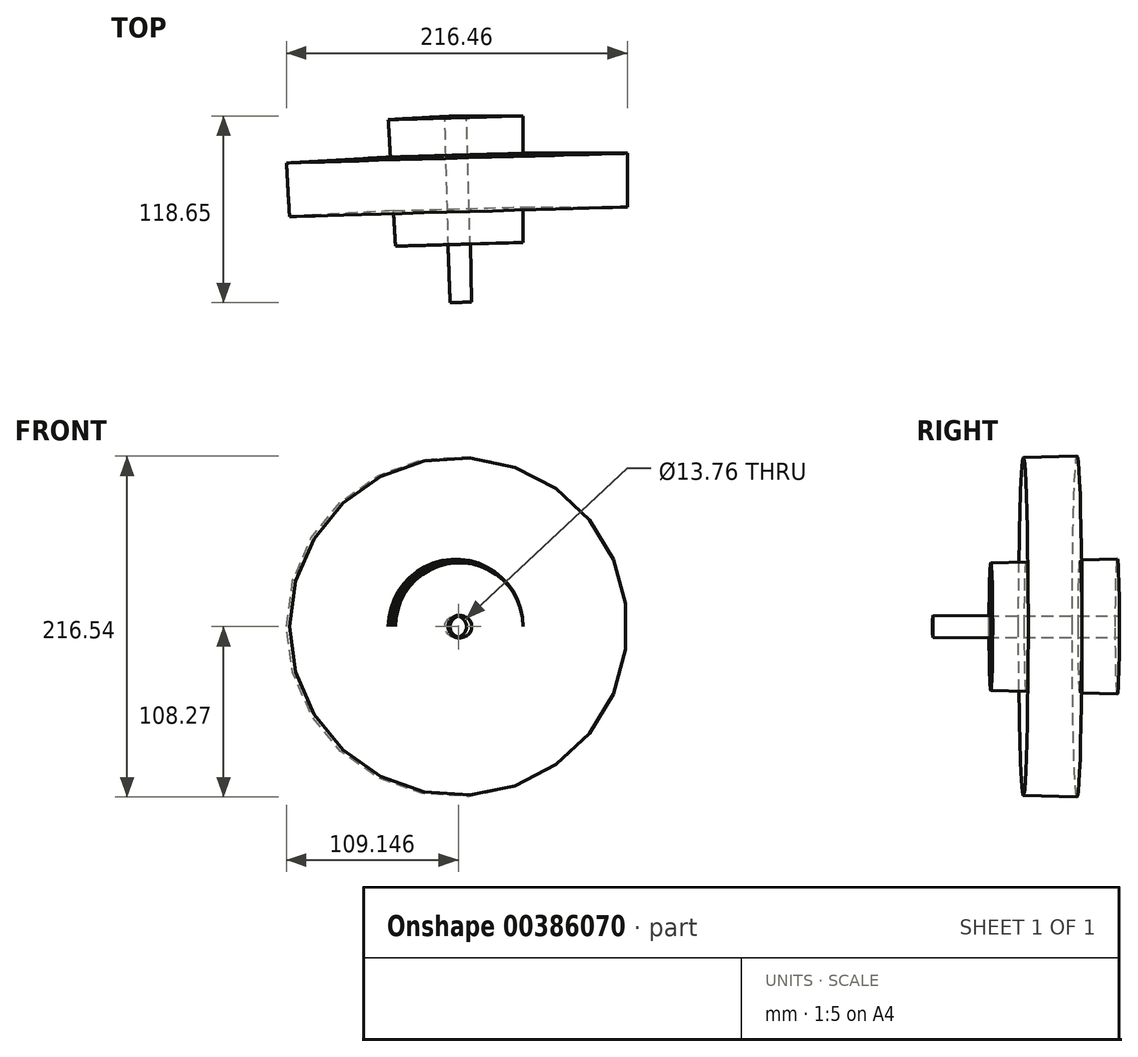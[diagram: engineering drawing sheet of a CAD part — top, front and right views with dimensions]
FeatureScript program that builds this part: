
annotation { "Feature Type Name" : "Feature", "Feature Type Description" : "" }
export const myFeature = defineFeature(function(context is Context, id is Id, definition is map)
    precondition{}
    {
        {
            var Q0;
            Q0=qCreatedBy(makeId("Top.planeOp"),FACE);
            var sketch = newSketch(context, id + "F0", { "sketchPlane" : qUnion([Q0])});
            skLineSegment(sketch, "E0", {"start": v(-49.07, 42.21) * mm, "end": v(-13.1, 42.21) * mm});
            skLineSegment(sketch, "E1", {"start": v(-13.1, 42.21) * mm, "end": v(-13.1, 18.44) * mm});
            skLineSegment(sketch, "E2", {"start": v(-13.1, 18.44) * mm, "end": v(53.04, 18.44) * mm});
            skLineSegment(sketch, "E3", {"start": v(53.04, 18.44) * mm, "end": v(53.04, -15.7) * mm});
            skLineSegment(sketch, "E4", {"start": v(53.04, -15.7) * mm, "end": v(-13.1, -15.7) * mm});
            skLineSegment(sketch, "E5", {"start": v(-13.1, -15.7) * mm, "end": v(-13.1, -38.25) * mm});
            skLineSegment(sketch, "E6", {"start": v(-45.72, -76.05) * mm, "end": v(-49.07, 42.21) * mm});
            skLineSegment(sketch, "E7", {"start": v(-56.5, 61.53) * mm, "end": v(-52.68, -73.4) * mm});
            skPoint(sketch, "E8.end.orphan", {"position": v(0, -38.25) * mm});
            skLineSegment(sketch, "E9", {"start": v(-46.76, -39.2) * mm, "end": v(-45.72, -76.05) * mm});
            skLineSegment(sketch, "E10", {"start": v(-13.1, -38.25) * mm, "end": v(-46.46, -39.2) * mm});
            skLineSegment(sketch, "E11", {"start": v(-46.46, -39.2) * mm, "end": v(-45.72, -76.05) * mm});
            skSolve(sketch);
        }
        {
            var Q0;
            Q0=makeQuery(id+"F0.imprint","IMPRINT",FACE,{"disambiguationData":[TD([[makeQuery(id+"F0.imprint","IMPRINT",EDGE,{"derivedFrom":sQuery(id+"F0.wireOp",EDGE,"E0")}),-1.0]])]});
            var Q1;
            Q1=sQuery(id+"F0.wireOp",EDGE,"E7");
            revolve(context, id + "F1", {"entities" : qUnion([Q0]), "axis" : qUnion([Q1]), "revolveType" : RevolveType.FULL});
        }
    });
